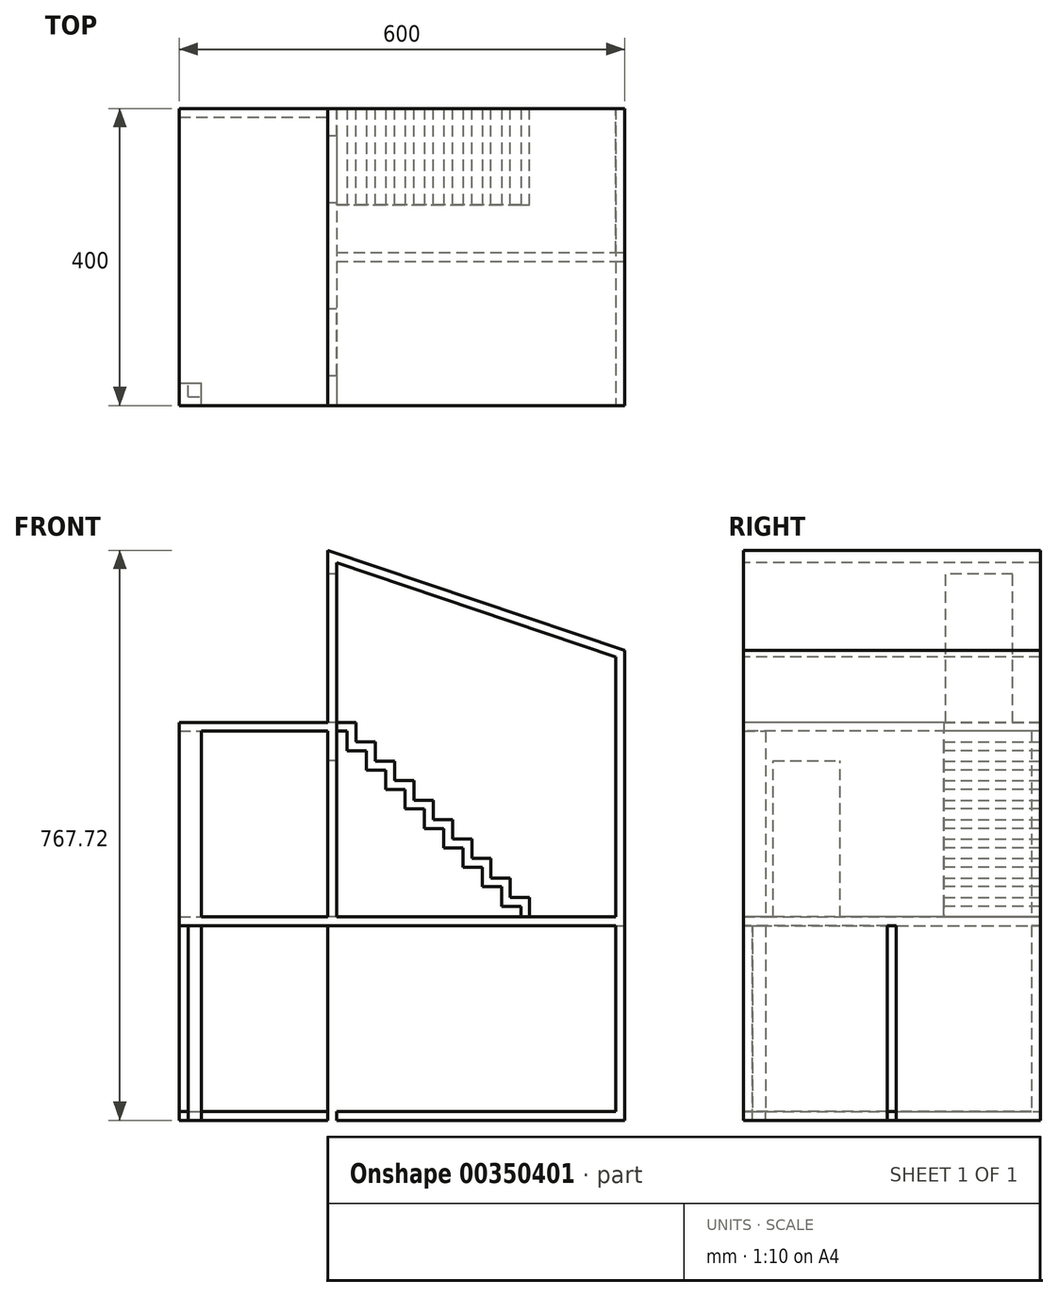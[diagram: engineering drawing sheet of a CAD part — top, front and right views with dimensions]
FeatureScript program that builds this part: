
annotation { "Feature Type Name" : "Feature", "Feature Type Description" : "" }
export const myFeature = defineFeature(function(context is Context, id is Id, definition is map)
    precondition{}
    {
        {
            var Q0;
            Q0=qCreatedBy(makeId("Top.planeOp"),FACE);
            var sketch = newSketch(context, id + "F0", { "sketchPlane" : qUnion([Q0])});
            skLineSegment(sketch, "E0.bottom", {"start": v(0, 0) * mm, "end": v(600, 0) * mm});
            skLineSegment(sketch, "E0.top", {"start": v(0, 400) * mm, "end": v(600, 400) * mm});
            skLineSegment(sketch, "E0.left", {"start": v(0, 0) * mm, "end": v(0, 400) * mm});
            skLineSegment(sketch, "E0.right", {"start": v(600, 0) * mm, "end": v(600, 400) * mm});
            skLineSegment(sketch, "E1.0", {"start": v(12, 388) * mm, "end": v(588, 388) * mm});
            skLineSegment(sketch, "E1.1", {"start": v(12, 12) * mm, "end": v(12, 388) * mm});
            skLineSegment(sketch, "E1.2", {"start": v(12, 12) * mm, "end": v(588, 12) * mm});
            skLineSegment(sketch, "E1.3", {"start": v(588, 12) * mm, "end": v(588, 388) * mm});
            skLineSegment(sketch, "E2.bottom", {"start": v(0, 0) * mm, "end": v(30, 0) * mm});
            skLineSegment(sketch, "E2.top", {"start": v(0, 30) * mm, "end": v(30, 30) * mm});
            skLineSegment(sketch, "E2.left", {"start": v(0, 0) * mm, "end": v(0, 30) * mm});
            skLineSegment(sketch, "E2.right", {"start": v(30, 0) * mm, "end": v(30, 30) * mm});
            skLineSegment(sketch, "E3.bottom", {"start": v(200, 400) * mm, "end": v(212, 400) * mm});
            skLineSegment(sketch, "E3.top", {"start": v(200, 0) * mm, "end": v(212, 0) * mm});
            skLineSegment(sketch, "E3.left", {"start": v(200, 400) * mm, "end": v(200, 0) * mm});
            skLineSegment(sketch, "E3.right", {"start": v(212, 400) * mm, "end": v(212, 0) * mm});
            skLineSegment(sketch, "E4.bottom", {"start": v(212, 194) * mm, "end": v(600, 194) * mm});
            skLineSegment(sketch, "E4.top", {"start": v(212, 206) * mm, "end": v(600, 206) * mm});
            skLineSegment(sketch, "E4.left", {"start": v(212, 194) * mm, "end": v(212, 206) * mm});
            skLineSegment(sketch, "E4.right", {"start": v(600, 194) * mm, "end": v(600, 206) * mm});
            skLineSegment(sketch, "E5", {"start": v(12, 388) * mm, "end": v(0, 388) * mm});
            skLineSegment(sketch, "E6", {"start": v(588, 388) * mm, "end": v(588, 400) * mm});
            skLineSegment(sketch, "E7", {"start": v(588, 12) * mm, "end": v(588, 0) * mm});
            skSolve(sketch);
        }
        {
            var Q0;
            {var subQ5=sQuery(id+"F0.wireOp",EDGE,"E0.left");Q0=makeQuery(id+"F0.imprint","IMPRINT",FACE,{"disambiguationData":[TD([[makeQuery(id+"F0.imprint","IMPRINT",EDGE,{"derivedFrom":subQ5}),-1.0]])]});}
            var Q1;
            {var subQ7=sQuery(id+"F0.wireOp",EDGE,"E1.1");var subQ9=sQuery(id+"F0.wireOp",EDGE,"E1.0");var subQ10=makeQuery(id+"F0.imprint","INTERSECT",VERTEX,{"derivedFrom":[subQ9,subQ7]});Q1=makeQuery(id+"F0.imprint","IMPRINT",FACE,{"disambiguationData":[TD([[makeQuery(id+"F0.imprint","IMPRINT",EDGE,{"disambiguationData":[TD([[subQ10,-1.0]])],"derivedFrom":subQ9}),-1.0]])]});}
            var Q2;
            {var subQ0=sQuery(id+"F0.wireOp",EDGE,"E2.bottom");Q2=makeQuery(id+"F0.imprint","IMPRINT",FACE,{"disambiguationData":[TD([[makeQuery(id+"F0.imprint","IMPRINT",EDGE,{"derivedFrom":subQ0}),1.0]])]});}
            var Q3;
            {var subQ0=sQuery(id+"F0.wireOp",EDGE,"E1.2");var subQ1=sQuery(id+"F0.wireOp",EDGE,"E1.1");var subQ2=makeQuery(id+"F0.imprint","INTERSECT",VERTEX,{"derivedFrom":[subQ1,subQ0]});Q3=makeQuery(id+"F0.imprint","IMPRINT",FACE,{"disambiguationData":[TD([[makeQuery(id+"F0.imprint","IMPRINT",EDGE,{"disambiguationData":[TD([[subQ2,-1.0]])],"derivedFrom":subQ1}),-1.0]])]});}
            var Q4;
            {var subQ0=sQuery(id+"F0.wireOp",EDGE,"E2.right");var subQ5=sQuery(id+"F0.wireOp",EDGE,"E1.2");var subQ6=makeQuery(id+"F0.imprint","INTERSECT",VERTEX,{"derivedFrom":[subQ5,subQ0]});Q4=makeQuery(id+"F0.imprint","IMPRINT",FACE,{"disambiguationData":[TD([[makeQuery(id+"F0.imprint","IMPRINT",EDGE,{"disambiguationData":[TD([[subQ6,-1.0]])],"derivedFrom":subQ5}),-1.0]])]});}
            var Q5;
            {var subQ0=sQuery(id+"F0.wireOp",EDGE,"E4.left");Q5=makeQuery(id+"F0.imprint","IMPRINT",FACE,{"disambiguationData":[TD([[makeQuery(id+"F0.imprint","IMPRINT",EDGE,{"derivedFrom":subQ0}),1.0]])]});}
            var Q6;
            {var subQ5=sQuery(id+"F0.wireOp",EDGE,"E3.top");Q6=makeQuery(id+"F0.imprint","IMPRINT",FACE,{"disambiguationData":[TD([[makeQuery(id+"F0.imprint","IMPRINT",EDGE,{"derivedFrom":subQ5}),1.0]])]});}
            var Q7;
            {var subQ0=sQuery(id+"F0.wireOp",EDGE,"E1.3");var subQ1=sQuery(id+"F0.wireOp",EDGE,"E1.2");var subQ2=makeQuery(id+"F0.imprint","INTERSECT",VERTEX,{"derivedFrom":[subQ1,subQ0]});Q7=makeQuery(id+"F0.imprint","IMPRINT",FACE,{"disambiguationData":[TD([[makeQuery(id+"F0.imprint","IMPRINT",EDGE,{"disambiguationData":[TD([[subQ2,1.0]])],"derivedFrom":subQ1}),-1.0]])]});}
            var Q8;
            {var subQ0=sQuery(id+"F0.wireOp",EDGE,"E1.3");var subQ1=sQuery(id+"F0.wireOp",EDGE,"E1.2");var subQ2=makeQuery(id+"F0.imprint","INTERSECT",VERTEX,{"derivedFrom":[subQ1,subQ0]});Q8=makeQuery(id+"F0.imprint","IMPRINT",FACE,{"disambiguationData":[TD([[makeQuery(id+"F0.imprint","IMPRINT",EDGE,{"disambiguationData":[TD([[subQ2,1.0]])],"derivedFrom":subQ1}),1.0]])]});}
            var Q9;
            {var subQ5=sQuery(id+"F0.wireOp",EDGE,"E4.left");Q9=makeQuery(id+"F0.imprint","IMPRINT",FACE,{"disambiguationData":[TD([[makeQuery(id+"F0.imprint","IMPRINT",EDGE,{"derivedFrom":subQ5}),-1.0]])]});}
            var Q10;
            {var subQ0=sQuery(id+"F0.wireOp",EDGE,"E1.3");var subQ1=sQuery(id+"F0.wireOp",EDGE,"E1.0");var subQ2=makeQuery(id+"F0.imprint","INTERSECT",VERTEX,{"derivedFrom":[subQ1,subQ0]});Q10=makeQuery(id+"F0.imprint","IMPRINT",FACE,{"disambiguationData":[TD([[makeQuery(id+"F0.imprint","IMPRINT",EDGE,{"disambiguationData":[TD([[subQ2,1.0]])],"derivedFrom":subQ1}),-1.0]])]});}
            var Q11;
            {var subQ0=sQuery(id+"F0.wireOp",EDGE,"E1.3");var subQ1=sQuery(id+"F0.wireOp",EDGE,"E1.0");var subQ2=makeQuery(id+"F0.imprint","INTERSECT",VERTEX,{"derivedFrom":[subQ1,subQ0]});Q11=makeQuery(id+"F0.imprint","IMPRINT",FACE,{"disambiguationData":[TD([[makeQuery(id+"F0.imprint","IMPRINT",EDGE,{"disambiguationData":[TD([[subQ2,1.0]])],"derivedFrom":subQ1}),1.0]])]});}
            var Q12;
            {var subQ5=sQuery(id+"F0.wireOp",EDGE,"E4.right");Q12=makeQuery(id+"F0.imprint","IMPRINT",FACE,{"disambiguationData":[TD([[makeQuery(id+"F0.imprint","IMPRINT",EDGE,{"derivedFrom":subQ5}),1.0]])]});}
            var Q13;
            {var subQ5=sQuery(id+"F0.wireOp",EDGE,"E3.bottom");Q13=makeQuery(id+"F0.imprint","IMPRINT",FACE,{"disambiguationData":[TD([[makeQuery(id+"F0.imprint","IMPRINT",EDGE,{"derivedFrom":subQ5}),-1.0]])]});}
            var Q14;
            {var subQ5=sQuery(id+"F0.wireOp",EDGE,"E5");Q14=makeQuery(id+"F0.imprint","IMPRINT",FACE,{"disambiguationData":[TD([[makeQuery(id+"F0.imprint","IMPRINT",EDGE,{"derivedFrom":subQ5}),-1.0]])]});}
            var Q15;
            {var subQ0=sQuery(id+"F0.wireOp",EDGE,"E6");Q15=makeQuery(id+"F0.imprint","IMPRINT",FACE,{"disambiguationData":[TD([[makeQuery(id+"F0.imprint","IMPRINT",EDGE,{"derivedFrom":subQ0}),-1.0]])]});}
            var Q16;
            {var subQ0=sQuery(id+"F0.wireOp",EDGE,"E7");Q16=makeQuery(id+"F0.imprint","IMPRINT",FACE,{"disambiguationData":[TD([[makeQuery(id+"F0.imprint","IMPRINT",EDGE,{"derivedFrom":subQ0}),1.0]])]});}
            extrude(context, id + "F1", {"entities" : qUnion([Q0, Q1, Q2, Q3, Q4, Q5, Q6, Q7, Q8, Q9, Q10, Q11, Q12, Q13, Q14, Q15, Q16]), "oppositeDirection" : true, "depth" : 12 * mm});
        }
        {
            var Q0;
            {var subQ5=sQuery(id+"F0.wireOp",EDGE,"E5");Q0=makeQuery(id+"F0.imprint","IMPRINT",FACE,{"disambiguationData":[TD([[makeQuery(id+"F0.imprint","IMPRINT",EDGE,{"derivedFrom":subQ5}),-1.0]])]});}
            var Q1;
            {var subQ5=sQuery(id+"F0.wireOp",EDGE,"E3.bottom");Q1=makeQuery(id+"F0.imprint","IMPRINT",FACE,{"disambiguationData":[TD([[makeQuery(id+"F0.imprint","IMPRINT",EDGE,{"derivedFrom":subQ5}),-1.0]])]});}
            var Q2;
            {var subQ0=sQuery(id+"F0.wireOp",EDGE,"E4.left");Q2=makeQuery(id+"F0.imprint","IMPRINT",FACE,{"disambiguationData":[TD([[makeQuery(id+"F0.imprint","IMPRINT",EDGE,{"derivedFrom":subQ0}),1.0]])]});}
            var Q3;
            {var subQ5=sQuery(id+"F0.wireOp",EDGE,"E3.top");Q3=makeQuery(id+"F0.imprint","IMPRINT",FACE,{"disambiguationData":[TD([[makeQuery(id+"F0.imprint","IMPRINT",EDGE,{"derivedFrom":subQ5}),1.0]])]});}
            var Q4;
            {var subQ0=sQuery(id+"F0.wireOp",EDGE,"E1.2");var subQ1=sQuery(id+"F0.wireOp",EDGE,"E1.1");var subQ2=makeQuery(id+"F0.imprint","INTERSECT",VERTEX,{"derivedFrom":[subQ1,subQ0]});Q4=makeQuery(id+"F0.imprint","IMPRINT",FACE,{"disambiguationData":[TD([[makeQuery(id+"F0.imprint","IMPRINT",EDGE,{"disambiguationData":[TD([[subQ2,-1.0]])],"derivedFrom":subQ1}),-1.0]])]});}
            var Q5;
            {var subQ0=sQuery(id+"F0.wireOp",EDGE,"E2.bottom");Q5=makeQuery(id+"F0.imprint","IMPRINT",FACE,{"disambiguationData":[TD([[makeQuery(id+"F0.imprint","IMPRINT",EDGE,{"derivedFrom":subQ0}),1.0]])]});}
            var Q6;
            {var subQ5=sQuery(id+"F0.wireOp",EDGE,"E4.left");Q6=makeQuery(id+"F0.imprint","IMPRINT",FACE,{"disambiguationData":[TD([[makeQuery(id+"F0.imprint","IMPRINT",EDGE,{"derivedFrom":subQ5}),-1.0]])]});}
            var Q7;
            {var subQ5=sQuery(id+"F0.wireOp",EDGE,"E4.right");Q7=makeQuery(id+"F0.imprint","IMPRINT",FACE,{"disambiguationData":[TD([[makeQuery(id+"F0.imprint","IMPRINT",EDGE,{"derivedFrom":subQ5}),1.0]])]});}
            var Q8;
            {var subQ0=sQuery(id+"F0.wireOp",EDGE,"E6");Q8=makeQuery(id+"F0.imprint","IMPRINT",FACE,{"disambiguationData":[TD([[makeQuery(id+"F0.imprint","IMPRINT",EDGE,{"derivedFrom":subQ0}),-1.0]])]});}
            var Q9;
            {var subQ0=sQuery(id+"F0.wireOp",EDGE,"E7");Q9=makeQuery(id+"F0.imprint","IMPRINT",FACE,{"disambiguationData":[TD([[makeQuery(id+"F0.imprint","IMPRINT",EDGE,{"derivedFrom":subQ0}),1.0]])]});}
            extrude(context, id + "F2", {"entities" : qUnion([Q0, Q1, Q2, Q3, Q4, Q5, Q6, Q7, Q8, Q9]), "operationType" : NewBodyOperationType.ADD, "depth" : 250 * mm});
        }
        {
            var Q0;
            Q0=makeQuery(id+"F2.opExtrude","SWEPT_FACE",FACE,{"disambiguationData":[OSD([sQuery(id+"F0.wireOp",EDGE,"E4.bottom")])]});
            var sketch = newSketch(context, id + "F3", { "sketchPlane" : qUnion([Q0])});
            skLineSegment(sketch, "E8.bottom", {"start": v(252, 0) * mm, "end": v(342, 0) * mm});
            skLineSegment(sketch, "E8.top", {"start": v(252, 210) * mm, "end": v(342, 210) * mm});
            skLineSegment(sketch, "E8.left", {"start": v(252, 0) * mm, "end": v(252, 210) * mm});
            skLineSegment(sketch, "E8.right", {"start": v(342, 0) * mm, "end": v(342, 210) * mm});
            skSolve(sketch);
        }
        {
            var Q0;
            Q0=makeQuery(id+"F3.imprint","IMPRINT",FACE,{"disambiguationData":[TD([[makeQuery(id+"F3.imprint","IMPRINT",EDGE,{"derivedFrom":sQuery(id+"F3.wireOp",EDGE,"E8.bottom")}),1.0]])]});
            extrude(context, id + "F4", {"entities" : qUnion([Q0]), "operationType" : NewBodyOperationType.REMOVE, "endBound" : BoundingType.THROUGH_ALL, "oppositeDirection" : true, "depth" : 259 * mm});
        }
        {
            var Q0;
            Q0=makeQuery(id+"F2.opExtrude","SWEPT_FACE",FACE,{"disambiguationData":[OSD([sQuery(id+"F0.wireOp",EDGE,"E3.left")])]});
            var sketch = newSketch(context, id + "F5", { "sketchPlane" : qUnion([Q0])});
            skLineSegment(sketch, "E9.bottom", {"start": v(-130, 0) * mm, "end": v(-40, 0) * mm});
            skLineSegment(sketch, "E9.top", {"start": v(-130, 210) * mm, "end": v(-40, 210) * mm});
            skLineSegment(sketch, "E9.left", {"start": v(-130, 0) * mm, "end": v(-130, 210) * mm});
            skLineSegment(sketch, "E9.right", {"start": v(-40, 0) * mm, "end": v(-40, 210) * mm});
            skSolve(sketch);
        }
        {
            var Q0;
            Q0=makeQuery(id+"F5.imprint","IMPRINT",FACE,{"disambiguationData":[TD([[makeQuery(id+"F5.imprint","IMPRINT",EDGE,{"derivedFrom":sQuery(id+"F5.wireOp",EDGE,"E9.bottom")}),1.0]])]});
            extrude(context, id + "F6", {"entities" : qUnion([Q0]), "operationType" : NewBodyOperationType.REMOVE, "oppositeDirection" : true, "depth" : 25 * mm});
        }
        {
            var Q0;
            Q0=makeQuery(id+"F2.opExtrude","CAP_FACE",FACE,{"disambiguationData":[OSD([sQuery(id+"F0.wireOp",EDGE,"E0.bottom"),sQuery(id+"F0.wireOp",EDGE,"E0.top"),sQuery(id+"F0.wireOp",EDGE,"E0.left"),sQuery(id+"F0.wireOp",EDGE,"E0.right"),sQuery(id+"F0.wireOp",EDGE,"E1.0"),sQuery(id+"F0.wireOp",EDGE,"E1.3"),sQuery(id+"F0.wireOp",EDGE,"E3.bottom"),sQuery(id+"F0.wireOp",EDGE,"E3.top"),sQuery(id+"F0.wireOp",EDGE,"E3.left"),sQuery(id+"F0.wireOp",EDGE,"E3.right"),sQuery(id+"F0.wireOp",EDGE,"E4.bottom"),sQuery(id+"F0.wireOp",EDGE,"E4.top"),sQuery(id+"F0.wireOp",EDGE,"E4.right"),sQuery(id+"F0.wireOp",EDGE,"E5"),sQuery(id+"F0.wireOp",EDGE,"E6"),sQuery(id+"F0.wireOp",EDGE,"E7")])],"isStart":false});
            var sketch = newSketch(context, id + "F7", { "sketchPlane" : qUnion([Q0])});
            skLineSegment(sketch, "E10.bottom", {"start": v(0, 0) * mm, "end": v(600, 0) * mm});
            skLineSegment(sketch, "E10.top", {"start": v(0, 400) * mm, "end": v(600, 400) * mm});
            skLineSegment(sketch, "E10.left", {"start": v(0, 0) * mm, "end": v(0, 400) * mm});
            skLineSegment(sketch, "E10.right", {"start": v(600, 0) * mm, "end": v(600, 400) * mm});
            skSolve(sketch);
        }
        {
            var Q0;
            Q0 = qSketchRegion(id + "F7", true);
            extrude(context, id + "F8", {"entities" : qUnion([Q0]), "operationType" : NewBodyOperationType.ADD, "depth" : 12 * mm});
        }
        {
            var Q0;
            Q0=makeQuery(id+"F8.opExtrude","CAP_FACE",FACE,{"disambiguationData":[OSD([sQuery(id+"F7.wireOp",EDGE,"E10.bottom"),sQuery(id+"F7.wireOp",EDGE,"E10.top"),sQuery(id+"F7.wireOp",EDGE,"E10.left"),sQuery(id+"F7.wireOp",EDGE,"E10.right")])],"isStart":false});
            var sketch = newSketch(context, id + "F9", { "sketchPlane" : qUnion([Q0])});
            skLineSegment(sketch, "E11.bottom", {"start": v(0, 400) * mm, "end": v(212, 400) * mm});
            skLineSegment(sketch, "E11.top", {"start": v(0, 388) * mm, "end": v(212, 388) * mm});
            skLineSegment(sketch, "E11.left", {"start": v(0, 400) * mm, "end": v(0, 388) * mm});
            skLineSegment(sketch, "E11.right", {"start": v(212, 400) * mm, "end": v(212, 388) * mm});
            skLineSegment(sketch, "E12.bottom", {"start": v(212, 388) * mm, "end": v(200, 388) * mm});
            skLineSegment(sketch, "E12.top", {"start": v(212, 0) * mm, "end": v(200, 0) * mm});
            skLineSegment(sketch, "E12.left", {"start": v(212, 388) * mm, "end": v(212, 0) * mm});
            skLineSegment(sketch, "E12.right", {"start": v(200, 388) * mm, "end": v(200, 0) * mm});
            skLineSegment(sketch, "E13.bottom", {"start": v(0, 0) * mm, "end": v(30, 0) * mm});
            skLineSegment(sketch, "E13.top", {"start": v(0, 30) * mm, "end": v(30, 30) * mm});
            skLineSegment(sketch, "E13.left", {"start": v(0, 0) * mm, "end": v(0, 30) * mm});
            skLineSegment(sketch, "E13.right", {"start": v(30, 0) * mm, "end": v(30, 30) * mm});
            skLineSegment(sketch, "E14.bottom", {"start": v(600, 400) * mm, "end": v(588, 400) * mm});
            skLineSegment(sketch, "E14.top", {"start": v(600, 0) * mm, "end": v(588, 0) * mm});
            skLineSegment(sketch, "E14.left", {"start": v(600, 400) * mm, "end": v(600, 0) * mm});
            skLineSegment(sketch, "E14.right", {"start": v(588, 400) * mm, "end": v(588, 0) * mm});
            skLineSegment(sketch, "E15.bottom", {"start": v(588, 206) * mm, "end": v(408, 206) * mm});
            skLineSegment(sketch, "E15.top", {"start": v(588, 194) * mm, "end": v(408, 194) * mm});
            skLineSegment(sketch, "E15.left", {"start": v(588, 206) * mm, "end": v(588, 194) * mm});
            skLineSegment(sketch, "E15.right", {"start": v(408, 206) * mm, "end": v(408, 194) * mm});
            skLineSegment(sketch, "E16.bottom", {"start": v(408, 206) * mm, "end": v(396, 206) * mm});
            skLineSegment(sketch, "E16.top", {"start": v(408, 0) * mm, "end": v(396, 0) * mm});
            skLineSegment(sketch, "E16.left", {"start": v(408, 206) * mm, "end": v(408, 0) * mm});
            skLineSegment(sketch, "E16.right", {"start": v(396, 206) * mm, "end": v(396, 0) * mm});
            skSolve(sketch);
        }
        {
            var Q0;
            {var subQ0=sQuery(id+"F0.wireOp",EDGE,"E3.top");var subQ1=sQuery(id+"F0.wireOp",EDGE,"E2.bottom");var subQ2=sQuery(id+"F0.wireOp",EDGE,"E0.bottom");Q0=makeQuery(id+"F8.boolean.opBoolean","MERGE",FACE,{"derivedFrom":[makeQuery(id+"F2.boolean.opBoolean","MERGE",FACE,{"derivedFrom":[makeQuery(id+"F1.opExtrude","SWEPT_FACE",FACE,{"disambiguationData":[OSD([subQ2,subQ1,subQ0])]}),makeQuery(id+"F2.opExtrude","SWEPT_FACE",FACE,{"disambiguationData":[OSD([subQ2])]}),makeQuery(id+"F2.opExtrude","SWEPT_FACE",FACE,{"disambiguationData":[OSD([subQ1])]}),makeQuery(id+"F2.opExtrude","SWEPT_FACE",FACE,{"disambiguationData":[OSD([subQ0])]})]}),makeQuery(id+"F8.opExtrude","SWEPT_FACE",FACE,{"disambiguationData":[OSD([sQuery(id+"F7.wireOp",EDGE,"E10.bottom")])]})]});}
            var sketch = newSketch(context, id + "F10", { "sketchPlane" : qUnion([Q0])});
            skLineSegment(sketch, "E17", {"start": v(0, 262) * mm, "end": v(0, 524) * mm});
            skLineSegment(sketch, "E18", {"start": v(0, 524) * mm, "end": v(200, 524) * mm});
            skLineSegment(sketch, "E19", {"start": v(200, 524) * mm, "end": v(200, 755.72) * mm});
            skLineSegment(sketch, "E20", {"start": v(200, 755.72) * mm, "end": v(600, 620.61) * mm});
            skLineSegment(sketch, "E21", {"start": v(600, 620.61) * mm, "end": v(600, 262) * mm});
            skLineSegment(sketch, "E22", {"start": v(600, 262) * mm, "end": v(588, 262) * mm});
            skLineSegment(sketch, "E23", {"start": v(588, 262) * mm, "end": v(588, 612) * mm});
            skLineSegment(sketch, "E24", {"start": v(588, 612) * mm, "end": v(212, 739) * mm});
            skLineSegment(sketch, "E25", {"start": v(212, 739) * mm, "end": v(212, 262) * mm});
            skLineSegment(sketch, "E26", {"start": v(212, 262) * mm, "end": v(0, 262) * mm});
            skLineSegment(sketch, "E27", {"start": v(12, 262) * mm, "end": v(12, 512) * mm});
            skLineSegment(sketch, "E28", {"start": v(12, 512) * mm, "end": v(200, 512) * mm});
            skLineSegment(sketch, "E29", {"start": v(200, 512) * mm, "end": v(200, 262) * mm});
            skLineSegment(sketch, "E30.bottom", {"start": v(442.07, 283) * mm, "end": v(417.07, 283) * mm});
            skLineSegment(sketch, "E30.top", {"start": v(442.07, 271) * mm, "end": v(417.07, 271) * mm});
            skLineSegment(sketch, "E30.left", {"start": v(442.07, 283) * mm, "end": v(442.07, 271) * mm});
            skLineSegment(sketch, "E30.right", {"start": v(417.07, 283) * mm, "end": v(417.07, 271) * mm});
            skLineSegment(sketch, "E31", {"start": v(450.26, 262) * mm, "end": v(212, 524) * mm});
            skPoint(sketch, "E31.endSnap0", {"position": v(212, 500.5) * mm});
            skLineSegment(sketch, "E32", {"start": v(12, 512) * mm, "end": v(0, 512) * mm});
            skSolve(sketch);
        }
        {
            var Q0;
            {var subQ5=sQuery(id+"F10.wireOp",EDGE,"E18");Q0=makeQuery(id+"F10.imprint","IMPRINT",FACE,{"disambiguationData":[TD([[makeQuery(id+"F10.imprint","IMPRINT",EDGE,{"derivedFrom":subQ5}),-1.0]])]});}
            extrude(context, id + "F11", {"entities" : qUnion([Q0]), "operationType" : NewBodyOperationType.ADD, "oppositeDirection" : true, "depth" : 400 * mm});
        }
        {
            var Q0;
            Q0=makeQuery(id+"F11.opExtrude","SWEPT_FACE",FACE,{"disambiguationData":[OSD([sQuery(id+"F10.wireOp",EDGE,"E29")])]});
            var sketch = newSketch(context, id + "F12", { "sketchPlane" : qUnion([Q0])});
            skLineSegment(sketch, "E33.bottom", {"start": v(-40, 262) * mm, "end": v(-130, 262) * mm});
            skLineSegment(sketch, "E33.top", {"start": v(-40, 472) * mm, "end": v(-130, 472) * mm});
            skLineSegment(sketch, "E33.left", {"start": v(-40, 262) * mm, "end": v(-40, 472) * mm});
            skLineSegment(sketch, "E33.right", {"start": v(-130, 262) * mm, "end": v(-130, 472) * mm});
            skLineSegment(sketch, "E34.bottom", {"start": v(-362.76, 524) * mm, "end": v(-272.76, 524) * mm});
            skLineSegment(sketch, "E34.top", {"start": v(-362.76, 724) * mm, "end": v(-272.76, 724) * mm});
            skLineSegment(sketch, "E34.left", {"start": v(-362.76, 524) * mm, "end": v(-362.76, 724) * mm});
            skLineSegment(sketch, "E34.right", {"start": v(-272.76, 524) * mm, "end": v(-272.76, 724) * mm});
            skLineSegment(sketch, "E35.0.0", {"start": v(0, 524) * mm, "end": v(0, 755.72) * mm});
            skLineSegment(sketch, "E35.0.1", {"start": v(0, 755.72) * mm, "end": v(-400, 755.72) * mm});
            skLineSegment(sketch, "E35.0.2", {"start": v(-400, 755.72) * mm, "end": v(-400, 524) * mm});
            skLineSegment(sketch, "E35.0.3", {"start": v(-400, 524) * mm, "end": v(0, 524) * mm});
            skSolve(sketch);
        }
        {
            var Q0;
            Q0=makeQuery(id+"F12.imprint","IMPRINT",FACE,{"disambiguationData":[TD([[makeQuery(id+"F12.imprint","IMPRINT",EDGE,{"derivedFrom":sQuery(id+"F12.wireOp",EDGE,"E34.top")}),-1.0]])]});
            var Q1;
            Q1=makeQuery(id+"F12.imprint","IMPRINT",FACE,{"disambiguationData":[TD([[makeQuery(id+"F12.imprint","IMPRINT",EDGE,{"derivedFrom":sQuery(id+"F12.wireOp",EDGE,"E33.bottom")}),1.0]])]});
            extrude(context, id + "F13", {"entities" : qUnion([Q0, Q1]), "operationType" : NewBodyOperationType.REMOVE, "oppositeDirection" : true, "depth" : 20 * mm});
        }
        {
            var Q0;
            Q0=makeQuery(id+"F9.imprint","IMPRINT",FACE,{"disambiguationData":[TD([[makeQuery(id+"F9.imprint","IMPRINT",EDGE,{"derivedFrom":sQuery(id+"F9.wireOp",EDGE,"E13.bottom")}),1.0]])]});
            extrude(context, id + "F14", {"entities" : qUnion([Q0]), "operationType" : NewBodyOperationType.ADD, "depth" : 250 * mm});
        }
        {
            var Q0;
            Q0=makeQuery(id+"F9.imprint","IMPRINT",FACE,{"disambiguationData":[TD([[makeQuery(id+"F9.imprint","IMPRINT",EDGE,{"derivedFrom":sQuery(id+"F9.wireOp",EDGE,"E11.bottom")}),-1.0]])]});
            extrude(context, id + "F15", {"entities" : qUnion([Q0]), "operationType" : NewBodyOperationType.ADD, "depth" : 250 * mm});
        }
        {
            var Q0;
            {var subQ0=sQuery(id+"F0.wireOp",EDGE,"E0.top");var subQ1=sQuery(id+"F0.wireOp",EDGE,"E3.bottom");Q0=makeQuery(id+"F15.boolean.opBoolean","MERGE",FACE,{"derivedFrom":[makeQuery(id+"F11.boolean.opBoolean","MERGE",FACE,{"derivedFrom":[makeQuery(id+"F8.boolean.opBoolean","MERGE",FACE,{"derivedFrom":[makeQuery(id+"F2.boolean.opBoolean","MERGE",FACE,{"derivedFrom":[makeQuery(id+"F1.opExtrude","SWEPT_FACE",FACE,{"disambiguationData":[OSD([subQ0,subQ1])]}),makeQuery(id+"F2.opExtrude","SWEPT_FACE",FACE,{"disambiguationData":[OSD([subQ0,subQ1])]}),makeQuery(id+"F2.opExtrude","SWEPT_FACE",FACE,{"disambiguationData":[OSD([subQ0])]})]}),makeQuery(id+"F8.opExtrude","SWEPT_FACE",FACE,{"disambiguationData":[OSD([sQuery(id+"F7.wireOp",EDGE,"E10.top")])]})]}),makeQuery(id+"F11.opExtrude","CAP_FACE",FACE,{"disambiguationData":[OSD([sQuery(id+"F10.wireOp",EDGE,"E17"),sQuery(id+"F10.wireOp",EDGE,"E18"),sQuery(id+"F10.wireOp",EDGE,"E19"),sQuery(id+"F10.wireOp",EDGE,"E20"),sQuery(id+"F10.wireOp",EDGE,"E21"),sQuery(id+"F10.wireOp",EDGE,"E22"),sQuery(id+"F10.wireOp",EDGE,"E23"),sQuery(id+"F10.wireOp",EDGE,"E24"),sQuery(id+"F10.wireOp",EDGE,"E25"),sQuery(id+"F10.wireOp",EDGE,"E26"),sQuery(id+"F10.wireOp",EDGE,"E28"),sQuery(id+"F10.wireOp",EDGE,"E29"),sQuery(id+"F10.wireOp",EDGE,"E32")])],"isStart":false})]}),makeQuery(id+"F15.opExtrude","SWEPT_FACE",FACE,{"disambiguationData":[OSD([sQuery(id+"F9.wireOp",EDGE,"E11.bottom")])]})]});}
            var sketch = newSketch(context, id + "F16", { "sketchPlane" : qUnion([Q0])});
            skLineSegment(sketch, "E36", {"start": v(-212, 524) * mm, "end": v(-238, 524) * mm});
            skLineSegment(sketch, "E37", {"start": v(-238, 524) * mm, "end": v(-238, 497.8) * mm});
            skLineSegment(sketch, "E38", {"start": v(-238, 497.8) * mm, "end": v(-264, 497.8) * mm});
            skLineSegment(sketch, "E39", {"start": v(-264, 497.8) * mm, "end": v(-264, 471.6) * mm});
            skLineSegment(sketch, "E40", {"start": v(-264, 471.6) * mm, "end": v(-290, 471.6) * mm});
            skLineSegment(sketch, "E41", {"start": v(-290, 471.6) * mm, "end": v(-290, 445.4) * mm});
            skLineSegment(sketch, "E42", {"start": v(-290, 445.4) * mm, "end": v(-316, 445.4) * mm});
            skLineSegment(sketch, "E43", {"start": v(-316, 445.4) * mm, "end": v(-316, 419.2) * mm});
            skLineSegment(sketch, "E44", {"start": v(-316, 419.2) * mm, "end": v(-342, 419.2) * mm});
            skLineSegment(sketch, "E45", {"start": v(-342, 419.2) * mm, "end": v(-342, 393) * mm});
            skLineSegment(sketch, "E46", {"start": v(-342, 393) * mm, "end": v(-368, 393) * mm});
            skLineSegment(sketch, "E47", {"start": v(-368, 393) * mm, "end": v(-368, 366.8) * mm});
            skLineSegment(sketch, "E48", {"start": v(-368, 366.8) * mm, "end": v(-394, 366.8) * mm});
            skLineSegment(sketch, "E49", {"start": v(-394, 366.8) * mm, "end": v(-394, 340.6) * mm});
            skLineSegment(sketch, "E50", {"start": v(-394, 340.6) * mm, "end": v(-420, 340.6) * mm});
            skLineSegment(sketch, "E51", {"start": v(-420, 340.6) * mm, "end": v(-420, 314.4) * mm});
            skLineSegment(sketch, "E52", {"start": v(-420, 314.4) * mm, "end": v(-446, 314.4) * mm});
            skLineSegment(sketch, "E53", {"start": v(-446, 314.4) * mm, "end": v(-446, 288.2) * mm});
            skLineSegment(sketch, "E54", {"start": v(-446, 288.2) * mm, "end": v(-472, 288.2) * mm});
            skLineSegment(sketch, "E55", {"start": v(-472, 288.2) * mm, "end": v(-472, 262) * mm});
            skLineSegment(sketch, "E56.0", {"start": v(-212, 524) * mm, "end": v(-200, 524) * mm});
            skLineSegment(sketch, "E57", {"start": v(-472, 262) * mm, "end": v(-212, 262) * mm});
            skLineSegment(sketch, "E58", {"start": v(-212, 262) * mm, "end": v(-212, 524) * mm});
            skSolve(sketch);
        }
        {
            var Q0;
            Q0=makeQuery(id+"F16.imprint","IMPRINT",FACE,{"disambiguationData":[TD([[makeQuery(id+"F16.imprint","IMPRINT",EDGE,{"derivedFrom":sQuery(id+"F16.wireOp",EDGE,"E36")}),1.0]])]});
            extrude(context, id + "F17", {"entities" : qUnion([Q0]), "operationType" : NewBodyOperationType.ADD, "oppositeDirection" : true, "depth" : 130 * mm});
        }
        {
            var Q0;
            Q0=makeQuery(id+"F17.opExtrude","CAP_FACE",FACE,{"disambiguationData":[OSD([sQuery(id+"F16.wireOp",EDGE,"E36"),sQuery(id+"F16.wireOp",EDGE,"E37"),sQuery(id+"F16.wireOp",EDGE,"E38"),sQuery(id+"F16.wireOp",EDGE,"E39"),sQuery(id+"F16.wireOp",EDGE,"E40"),sQuery(id+"F16.wireOp",EDGE,"E41"),sQuery(id+"F16.wireOp",EDGE,"E42"),sQuery(id+"F16.wireOp",EDGE,"E43"),sQuery(id+"F16.wireOp",EDGE,"E44"),sQuery(id+"F16.wireOp",EDGE,"E45"),sQuery(id+"F16.wireOp",EDGE,"E46"),sQuery(id+"F16.wireOp",EDGE,"E47"),sQuery(id+"F16.wireOp",EDGE,"E48"),sQuery(id+"F16.wireOp",EDGE,"E49"),sQuery(id+"F16.wireOp",EDGE,"E50"),sQuery(id+"F16.wireOp",EDGE,"E51"),sQuery(id+"F16.wireOp",EDGE,"E52"),sQuery(id+"F16.wireOp",EDGE,"E53"),sQuery(id+"F16.wireOp",EDGE,"E54"),sQuery(id+"F16.wireOp",EDGE,"E55"),sQuery(id+"F16.wireOp",EDGE,"E57"),sQuery(id+"F16.wireOp",EDGE,"E58")])],"isStart":false});
            var sketch = newSketch(context, id + "F18", { "sketchPlane" : qUnion([Q0])});
            skLineSegment(sketch, "E59.0", {"start": v(460, 262) * mm, "end": v(460, 276.2) * mm});
            skLineSegment(sketch, "E59.3", {"start": v(226, 512) * mm, "end": v(212, 512) * mm});
            skLineSegment(sketch, "E59.4", {"start": v(226, 485.8) * mm, "end": v(226, 512) * mm});
            skLineSegment(sketch, "E59.5", {"start": v(460, 276.2) * mm, "end": v(434, 276.2) * mm});
            skLineSegment(sketch, "E59.6", {"start": v(252, 485.8) * mm, "end": v(226, 485.8) * mm});
            skLineSegment(sketch, "E59.7", {"start": v(252, 459.6) * mm, "end": v(252, 485.8) * mm});
            skLineSegment(sketch, "E59.8", {"start": v(278, 459.6) * mm, "end": v(252, 459.6) * mm});
            skLineSegment(sketch, "E59.9", {"start": v(278, 433.4) * mm, "end": v(278, 459.6) * mm});
            skLineSegment(sketch, "E59.10", {"start": v(304, 433.4) * mm, "end": v(278, 433.4) * mm});
            skLineSegment(sketch, "E59.11", {"start": v(304, 407.2) * mm, "end": v(304, 433.4) * mm});
            skLineSegment(sketch, "E59.12", {"start": v(408, 328.6) * mm, "end": v(382, 328.6) * mm});
            skLineSegment(sketch, "E59.13", {"start": v(408, 302.4) * mm, "end": v(408, 328.6) * mm});
            skLineSegment(sketch, "E59.14", {"start": v(434, 302.4) * mm, "end": v(408, 302.4) * mm});
            skLineSegment(sketch, "E59.15", {"start": v(434, 276.2) * mm, "end": v(434, 302.4) * mm});
            skLineSegment(sketch, "E59.16", {"start": v(382, 328.6) * mm, "end": v(382, 354.8) * mm});
            skLineSegment(sketch, "E59.17", {"start": v(382, 354.8) * mm, "end": v(356, 354.8) * mm});
            skLineSegment(sketch, "E59.18", {"start": v(356, 354.8) * mm, "end": v(356, 381) * mm});
            skLineSegment(sketch, "E59.19", {"start": v(356, 381) * mm, "end": v(330, 381) * mm});
            skLineSegment(sketch, "E59.20", {"start": v(330, 381) * mm, "end": v(330, 407.2) * mm});
            skLineSegment(sketch, "E59.21", {"start": v(330, 407.2) * mm, "end": v(304, 407.2) * mm});
            skSolve(sketch);
        }
        {
            var Q0;
            {var subQ0=sQuery(id+"F18.wireOp",EDGE,"E59.0");Q0=makeQuery(id+"F18.imprint","IMPRINT",FACE,{"disambiguationData":[TD([[makeQuery(id+"F18.imprint","IMPRINT",EDGE,{"derivedFrom":subQ0}),1.0]])]});}
            extrude(context, id + "F19", {"entities" : qUnion([Q0]), "operationType" : NewBodyOperationType.REMOVE, "oppositeDirection" : true, "depth" : 160 * mm});
        }
    });
